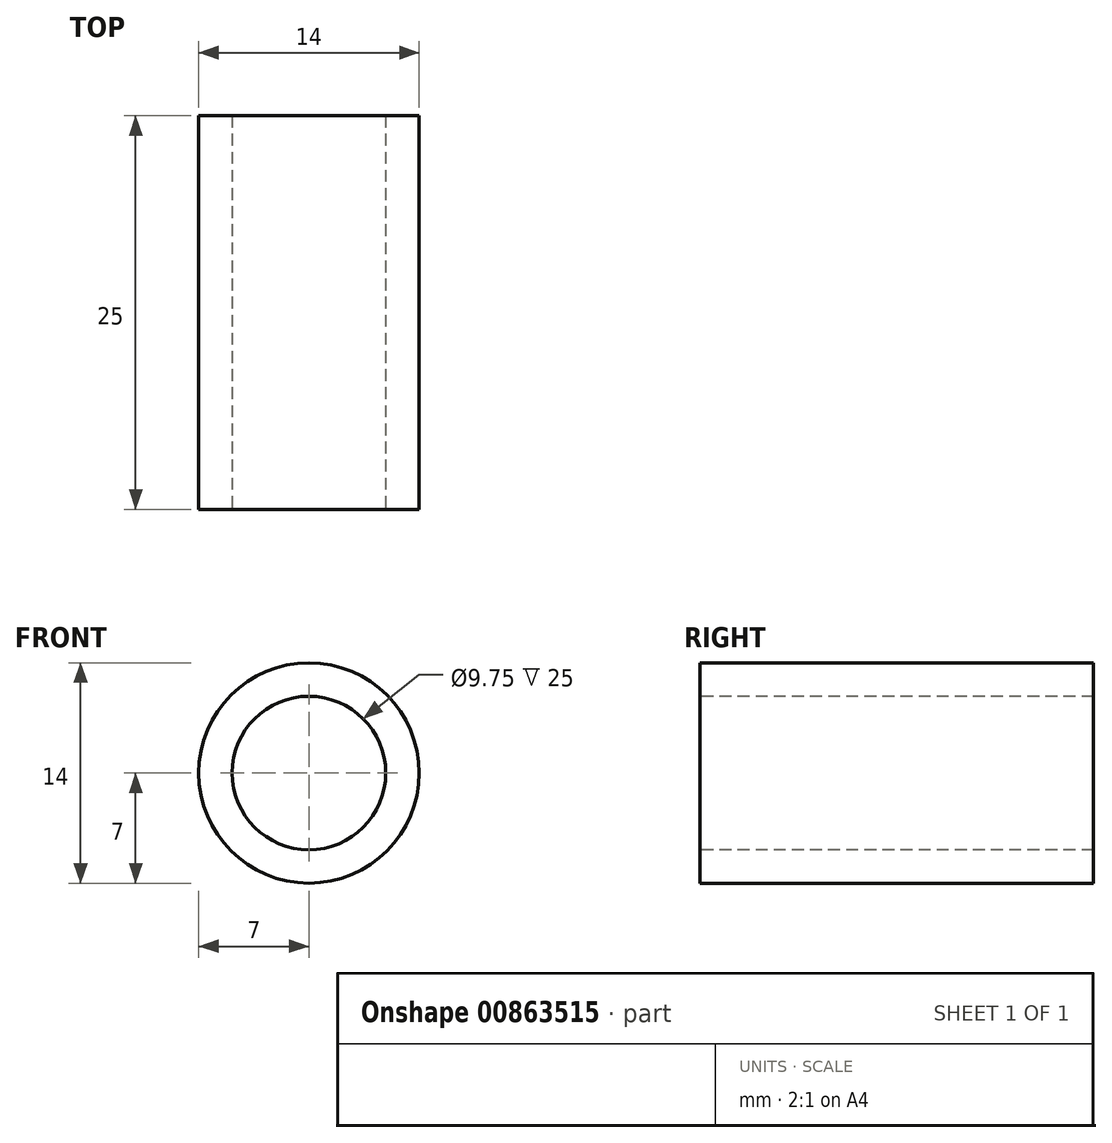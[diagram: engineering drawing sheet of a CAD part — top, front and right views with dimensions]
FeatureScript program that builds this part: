
annotation { "Feature Type Name" : "Feature", "Feature Type Description" : "" }
export const myFeature = defineFeature(function(context is Context, id is Id, definition is map)
    precondition{}
    {
        {
            var Q0;
            Q0=qCreatedBy(makeId("Front.planeOp"),FACE);
            var sketch = newSketch(context, id + "F0", { "sketchPlane" : qUnion([Q0])});
            skCircle(sketch, "E0", {"center": v(0, 0) * mm, "radius": 4.88 * mm});
            skCircle(sketch, "E1", {"center": v(0, 0) * mm, "radius": 7 * mm});
            skSolve(sketch);
        }
        {
            var Q0;
            Q0=makeQuery(id+"F0.imprint","IMPRINT",FACE,{"disambiguationData":[TD([[makeQuery(id+"F0.imprint","IMPRINT",EDGE,{"derivedFrom":sQuery(id+"F0.wireOp",EDGE,"E0")}),-1.0]])]});
            extrude(context, id + "F1", {"entities" : qUnion([Q0]), "oppositeDirection" : true, "depth" : 25 * mm, "offsetDistance" : 25 * mm});
        }
    });
